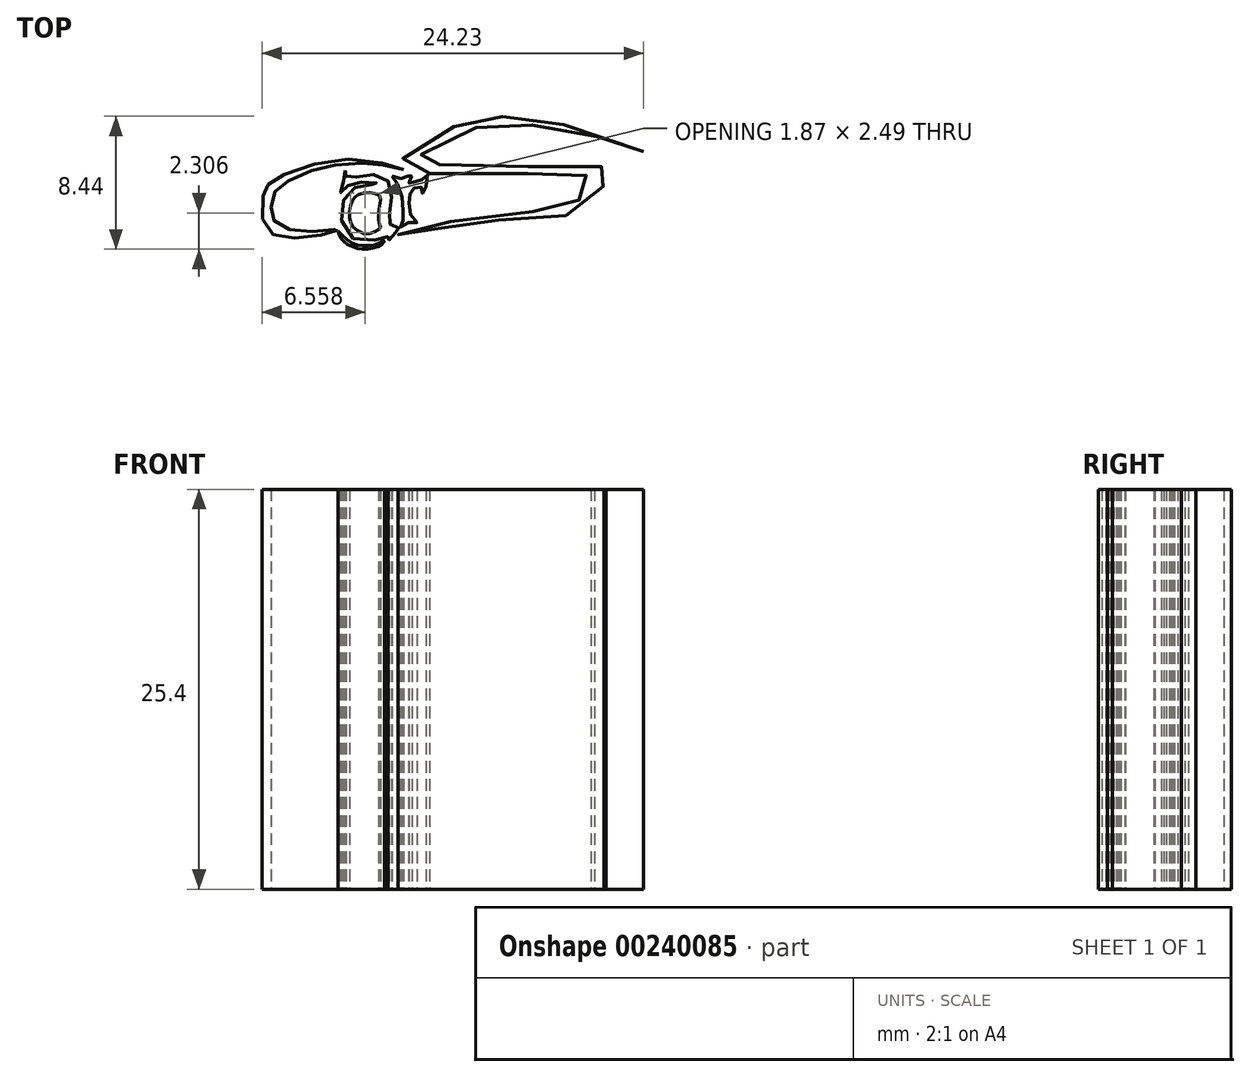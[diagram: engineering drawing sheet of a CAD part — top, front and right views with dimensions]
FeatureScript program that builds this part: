
annotation { "Feature Type Name" : "Feature", "Feature Type Description" : "" }
export const myFeature = defineFeature(function(context is Context, id is Id, definition is map)
    precondition{}
    {
        {
            var Q0;
            Q0=qCreatedBy(makeId("Top.planeOp"),FACE);
            var sketch = newSketch(context, id + "F0", { "sketchPlane" : qUnion([Q0])});
            skFitSpline(sketch, "E0", {"points": [v(-6.07, 1.66) * mm, v(-7.62, 2.13) * mm, v(-10.9, 2.2) * mm, v(-13.81, 1.28) * mm, v(-14.63, 0.76) * mm, v(-14.86, 0.5) * mm, v(-15.03, -0.27) * mm, v(-14.92, -1.8) * mm, v(-14.25, -2.5) * mm, v(-12.79, -2.66) * mm, v(-10.95, -2.43) * mm, v(-10.43, -2.24) * mm, v(-10.08, -2.02) * mm, v(-10.58, -2.17) * mm, v(-11.97, -2.25) * mm, v(-13.45, -2.1) * mm, v(-14.27, -1.63) * mm, v(-14.44, -1.05) * mm, v(-14.46, -0.54) * mm, v(-14.25, 0.24) * mm, v(-13.83, 0.7) * mm, v(-12.24, 1.47) * mm, v(-10.66, 1.92) * mm, v(-8.58, 2.09) * mm, v(-7.22, 1.94) * mm, v(-6.07, 1.66) * mm]});
            skFitSpline(sketch, "E1", {"points": [v(-9.8, 1.6) * mm, v(-9.91, 1.4) * mm, v(-9.89, 1.03) * mm, v(-9.9, 0.62) * mm, v(-10.07, 0.2) * mm, v(-9.9, 0.31) * mm, v(-9.67, 0.57) * mm, v(-9.5, 0.7) * mm, v(-9.08, 0.83) * mm, v(-8.2, 0.91) * mm, v(-7.83, 0.83) * mm, v(-7.6, 0.62) * mm, v(-8.1, 0.72) * mm, v(-8.77, 0.7) * mm, v(-9.62, 0.15) * mm, v(-9.93, -0.4) * mm, v(-10, -1.54) * mm, v(-9.39, -2.65) * mm, v(-8.25, -2.9) * mm, v(-7.2, -2.53) * mm, v(-7.07, -2.55) * mm, v(-7.09, -2.72) * mm, v(-7.22, -2.8) * mm, v(-7.04, -2.82) * mm, v(-6.82, -2.7) * mm, v(-6.65, -2.5) * mm, v(-6.47, -2.23) * mm, v(-6.2, -2.11) * mm, v(-6.31, -2.06) * mm, v(-6.63, -2.1) * mm, v(-6.87, -1.93) * mm, v(-6.96, -1.67) * mm, v(-6.97, -1.44) * mm, v(-6.95, -0.9) * mm, v(-6.86, -0.24) * mm, v(-6.88, 0.6) * mm, v(-7.22, 1.1) * mm, v(-7.87, 1.34) * mm, v(-8.75, 1.22) * mm, v(-9.3, 1.17) * mm, v(-9.54, 1.18) * mm, v(-9.76, 1.28) * mm, v(-9.79, 1.45) * mm, v(-9.72, 1.65) * mm, v(-9.8, 1.6) * mm]});
            skFitSpline(sketch, "E2", {"points": [v(-8.91, 0.1) * mm, v(-8.4, 0.2) * mm, v(-7.81, 0.14) * mm, v(-7.54, -0.08) * mm, v(-7.6, -0.7) * mm, v(-7.66, -1.48) * mm, v(-7.57, -1.92) * mm, v(-7.53, -2.02) * mm, v(-7.63, -2.12) * mm, v(-7.92, -2.3) * mm, v(-8.56, -2.4) * mm, v(-9.21, -2.05) * mm, v(-9.4, -1.8) * mm, v(-9.5, -1.15) * mm, v(-9.4, -0.46) * mm, v(-9.14, -0.05) * mm, v(-8.91, 0.1) * mm]});
            skFitSpline(sketch, "E3", {"points": [v(-10.16, -2.3) * mm, v(-9.43, -2.95) * mm, v(-8.57, -3.16) * mm, v(-7.66, -3.03) * mm, v(-7.29, -2.84) * mm, v(-7.43, -3.07) * mm, v(-8.18, -3.34) * mm, v(-8.95, -3.35) * mm, v(-9.68, -3.03) * mm, v(-10.09, -2.6) * mm, v(-10.24, -2.23) * mm, v(-10.16, -2.3) * mm]});
            skFitSpline(sketch, "E4", {"points": [v(-6.79, 1.26) * mm, v(-6.33, 1.14) * mm, v(-6.14, 1.1) * mm, v(-5.87, 1.2) * mm, v(-5.53, 1.42) * mm, v(-5.58, 1.23) * mm, v(-5.7, 0.93) * mm, v(-5.68, 0.76) * mm, v(-5.45, 0.86) * mm, v(-5.13, 0.95) * mm, v(-4.93, 1) * mm, v(-4.77, 1.15) * mm, v(-4.54, 1.33) * mm, v(-4.42, 1.36) * mm, v(-4.58, 1.12) * mm, v(-4.65, 0.76) * mm, v(-4.7, 0.35) * mm, v(-4.87, 0.14) * mm, v(-4.9, 0.4) * mm, v(-4.97, 0.56) * mm, v(-5.23, 0.57) * mm, v(-5.48, 0.43) * mm, v(-5.63, 0.2) * mm, v(-5.73, -0.12) * mm, v(-5.7, -0.66) * mm, v(-5.55, -1.36) * mm, v(-5.21, -1.7) * mm, v(-5.6, -1.69) * mm, v(-5.92, -1.78) * mm, v(-6.27, -1.97) * mm, v(-6.15, -1.72) * mm, v(-6.09, -1.44) * mm, v(-6.1, -0.8) * mm, v(-6.2, 0.18) * mm, v(-6.6, 0.97) * mm, v(-6.79, 1.26) * mm]});
            skFitSpline(sketch, "E5", {"points": [v(9.17, 2.8) * mm, v(5.66, 4.12) * mm, v(2.17, 4.85) * mm, v(0.45, 5.04) * mm, v(-0.93, 5) * mm, v(-1.68, 4.87) * mm, v(-4.4, 3.65) * mm, v(-5.84, 2.67) * mm, v(-6.2, 2.1) * mm, v(-5.94, 1.69) * mm, v(-5.54, 1.52) * mm, v(-3.06, 1.4) * mm, v(2.71, 1.41) * mm, v(4.87, 1.34) * mm, v(5.57, 1.28) * mm, v(5.82, 1.1) * mm, v(5.82, 0.76) * mm, v(5.54, 0.25) * mm, v(4.9, -0.41) * mm, v(4.14, -0.77) * mm, v(2.4, -1) * mm, v(-0.74, -1.28) * mm, v(-4.93, -1.9) * mm, v(-5.91, -2.11) * mm, v(-6.42, -2.5) * mm, v(-6.02, -2.29) * mm, v(-4.84, -2.11) * mm, v(-3.27, -2.01) * mm, v(-1.98, -1.75) * mm, v(1.96, -1.38) * mm, v(3.89, -1.25) * mm, v(4.93, -1.16) * mm, v(5.55, -0.78) * mm, v(6.63, 0.98) * mm, v(6.07, 1.56) * mm, v(6.8, 1.8) * mm, v(6.36, 1.88) * mm, v(3.5, 1.86) * mm, v(-0.64, 1.89) * mm, v(-4.46, 2.02) * mm, v(-5.08, 2.1) * mm, v(-5.2, 2.24) * mm, v(-5.2, 2.4) * mm, v(-4.96, 2.61) * mm, v(-4.29, 3.03) * mm, v(-1.55, 4.3) * mm, v(0.2, 4.57) * mm, v(2.06, 4.5) * mm, v(4.63, 4.13) * mm, v(6.65, 3.63) * mm, v(7.74, 3.31) * mm, v(9.17, 2.8) * mm]});
            skSolve(sketch);
        }
        {
            var Q0;
            Q0 = qSketchRegion(id + "F0", true);
            extrude(context, id + "F1", {"entities" : qUnion([Q0]), "depth" : 25.4 * mm});
        }
    });
